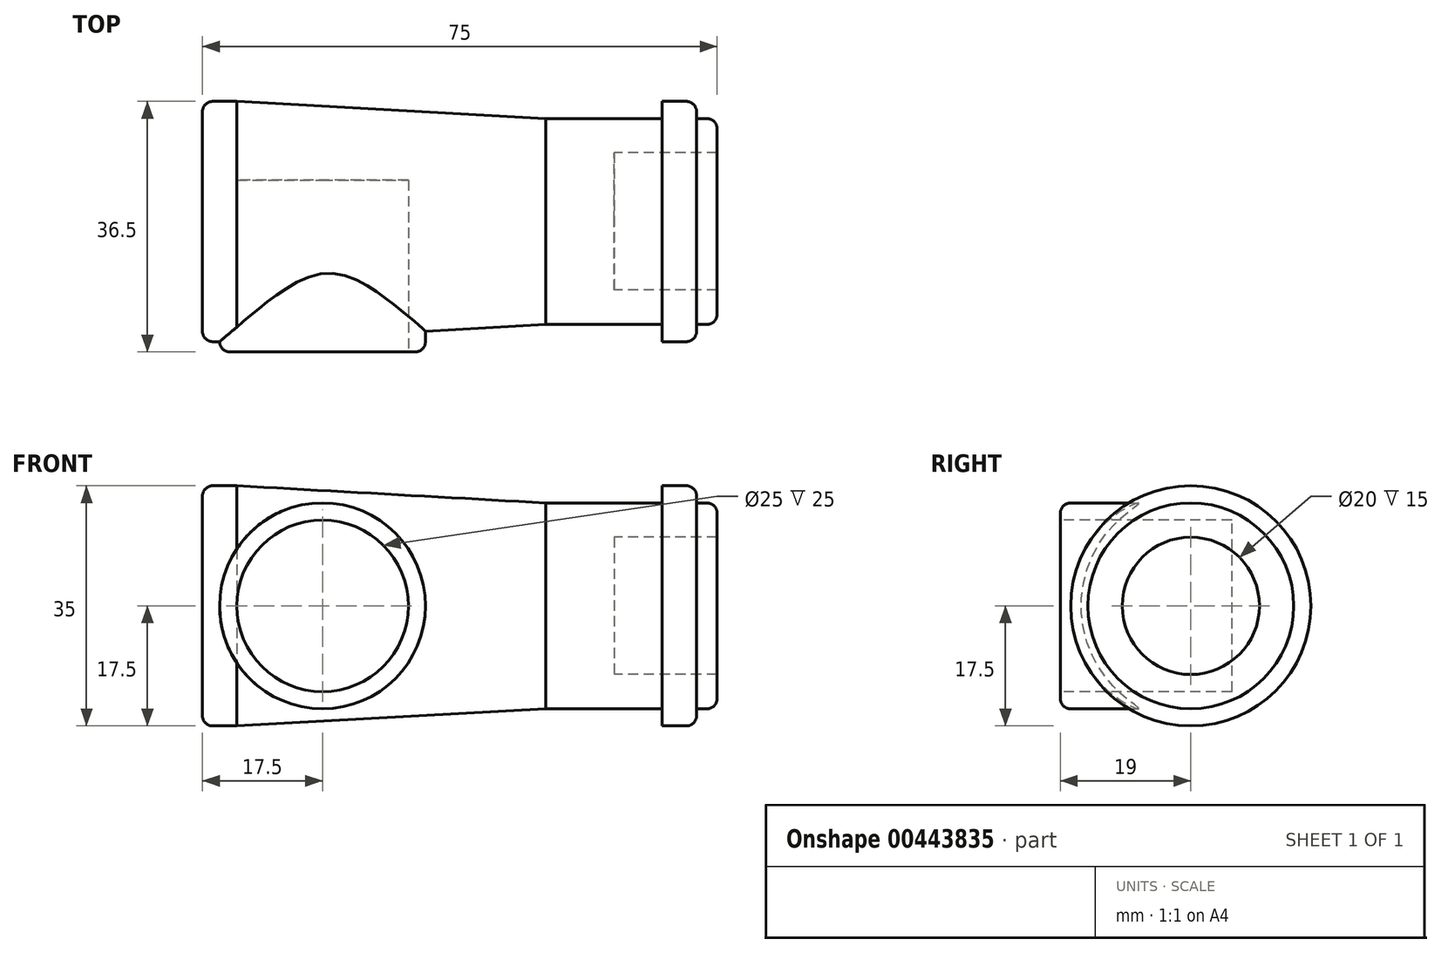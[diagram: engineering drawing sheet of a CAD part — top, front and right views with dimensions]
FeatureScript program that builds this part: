
annotation { "Feature Type Name" : "Feature", "Feature Type Description" : "" }
export const myFeature = defineFeature(function(context is Context, id is Id, definition is map)
    precondition{}
    {
        {
            var Q0;
            Q0=qCreatedBy(makeId("Front.planeOp"),FACE);
            var sketch = newSketch(context, id + "F0", { "sketchPlane" : qUnion([Q0])});
            skLineSegment(sketch, "E0", {"start": v(0, 0) * mm, "end": v(60, 0) * mm});
            skLineSegment(sketch, "E1", {"start": v(60, 0) * mm, "end": v(60, 10) * mm});
            skLineSegment(sketch, "E2", {"start": v(60, 10) * mm, "end": v(75, 10) * mm});
            skLineSegment(sketch, "E3", {"start": v(75, 10) * mm, "end": v(75, 15) * mm});
            skLineSegment(sketch, "E4", {"start": v(75, 15) * mm, "end": v(72, 15) * mm});
            skLineSegment(sketch, "E5", {"start": v(72, 15) * mm, "end": v(72, 17.5) * mm});
            skLineSegment(sketch, "E6", {"start": v(72, 17.5) * mm, "end": v(67, 17.5) * mm});
            skLineSegment(sketch, "E7", {"start": v(67, 17.5) * mm, "end": v(67, 15) * mm});
            skLineSegment(sketch, "E8", {"start": v(67, 15) * mm, "end": v(50, 15) * mm});
            skLineSegment(sketch, "E9", {"start": v(0, 17.5) * mm, "end": v(0, 0) * mm});
            skLineSegment(sketch, "E10", {"start": v(50, 15) * mm, "end": v(5, 17.5) * mm});
            skLineSegment(sketch, "E11", {"start": v(5, 17.5) * mm, "end": v(0, 17.5) * mm});
            skSolve(sketch);
        }
        {
            var Q0;
            Q0 = qSketchRegion(id + "F0", true);
            var Q1;
            Q1=sQuery(id+"F0.wireOp",EDGE,"E0");
            revolve(context, id + "F1", {"entities" : qUnion([Q0]), "axis" : qUnion([Q1]), "revolveType" : RevolveType.FULL});
        }
        {
            var Q0;
            Q0=qCreatedBy(makeId("Front.planeOp"),FACE);
            var sketch = newSketch(context, id + "F2", { "sketchPlane" : qUnion([Q0])});
            skCircle(sketch, "E12", {"center": v(17.5, 0) * mm, "radius": 15 * mm});
            skSolve(sketch);
        }
        {
            var Q0;
            Q0 = qSketchRegion(id + "F2", true);
            extrude(context, id + "F3", {"entities" : qUnion([Q0]), "operationType" : NewBodyOperationType.ADD, "depth" : 19 * mm});
        }
        {
            var Q0;
            Q0=makeQuery(id+"F3.opExtrude","CAP_FACE",FACE,{"disambiguationData":[OSD([sQuery(id+"F2.wireOp",EDGE,"E12")])],"isStart":false});
            var sketch = newSketch(context, id + "F4", { "sketchPlane" : qUnion([Q0])});
            skCircle(sketch, "E13", {"center": v(17.5, 0) * mm, "radius": 12.5 * mm});
            skSolve(sketch);
        }
        {
            var Q0;
            Q0 = qSketchRegion(id + "F4", true);
            extrude(context, id + "F5", {"entities" : qUnion([Q0]), "operationType" : NewBodyOperationType.REMOVE, "oppositeDirection" : true, "depth" : 25 * mm});
        }
        {
            var Q0;
            Q0=makeQuery(id+"F1.opRevolve","SWEPT_EDGE",EDGE,{"disambiguationData":[OSD([sQuery(id+"F0.wireOp",EDGE,"E5"),sQuery(id+"F0.wireOp",EDGE,"E6")])]});
            var Q1;
            Q1=makeQuery(id+"F1.opRevolve","SWEPT_EDGE",EDGE,{"disambiguationData":[OSD([sQuery(id+"F0.wireOp",EDGE,"E3"),sQuery(id+"F0.wireOp",EDGE,"E4")])]});
            var Q2;
            Q2=makeQuery(id+"F1.opRevolve","SWEPT_EDGE",EDGE,{"disambiguationData":[OSD([sQuery(id+"F0.wireOp",EDGE,"E9"),sQuery(id+"F0.wireOp",EDGE,"E11")])]});
            fillet(context, id + "F6", {"entities" : qUnion([Q0, Q1, Q2]), "radius" : 1.5 * mm, "tangentPropagation" : true, "allowEdgeOverflow" : false});
        }
        {
            var Q0;
            Q0=makeQuery(id+"F3.opExtrude","CAP_EDGE",EDGE,{"disambiguationData":[OSD([sQuery(id+"F2.wireOp",EDGE,"E12")])],"isStart":false});
            fillet(context, id + "F7", {"entities" : qUnion([Q0]), "radius" : 1.5 * mm, "tangentPropagation" : true, "allowEdgeOverflow" : false});
        }
    });
